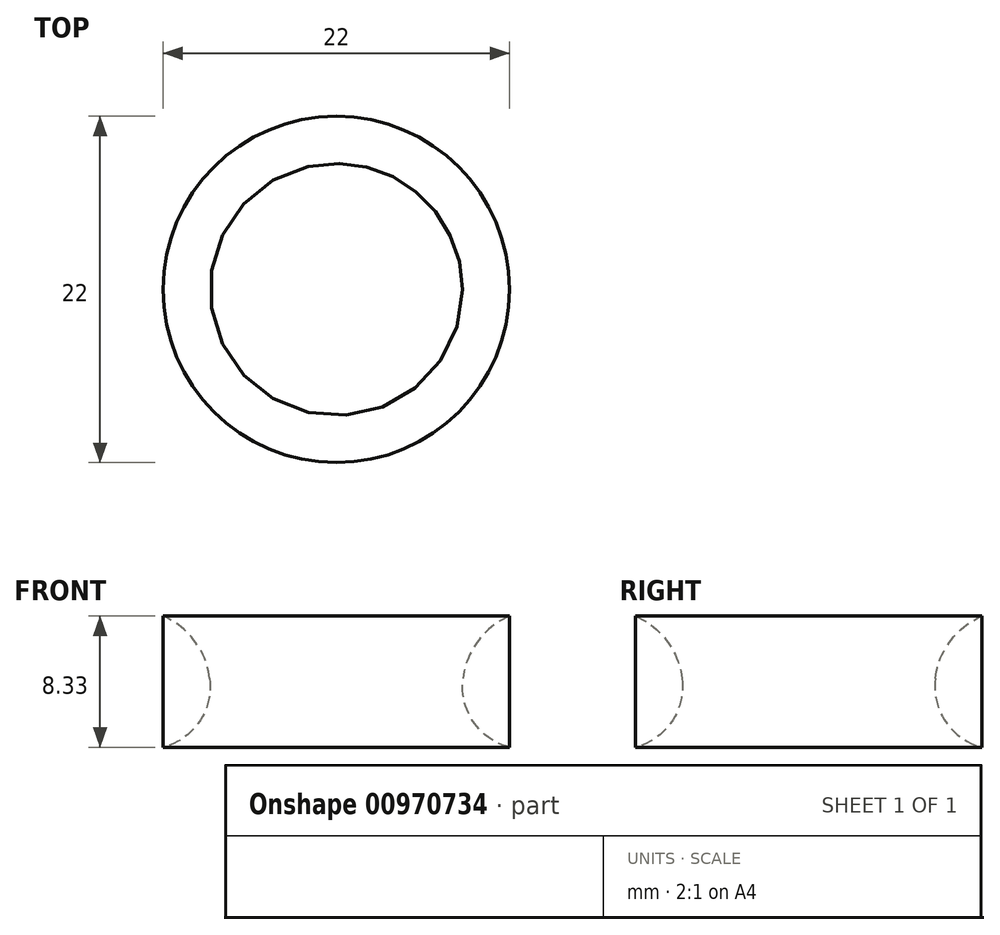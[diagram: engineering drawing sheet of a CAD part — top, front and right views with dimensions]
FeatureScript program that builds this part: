
annotation { "Feature Type Name" : "Feature", "Feature Type Description" : "" }
export const myFeature = defineFeature(function(context is Context, id is Id, definition is map)
    precondition{}
    {
        {
            var Q0;
            Q0=qCreatedBy(makeId("Top.planeOp"),FACE);
            var sketch = newSketch(context, id + "F0", { "sketchPlane" : qUnion([Q0])});
            skCircle(sketch, "E0", {"center": v(0, 0) * mm, "radius": 11 * mm});
            skCircle(sketch, "E1", {"center": v(0, 0) * mm, "radius": 8 * mm});
            skSolve(sketch);
        }
        {
            var Q0;
            Q0=makeQuery(id+"F0.imprint","IMPRINT",FACE,{"disambiguationData":[TD([[makeQuery(id+"F0.imprint","IMPRINT",EDGE,{"derivedFrom":sQuery(id+"F0.wireOp",EDGE,"E0")}),1.0]])]});
            extrude(context, id + "F1", {"entities" : qUnion([Q0]), "depth" : 8.33 * mm, "offsetDistance" : 25 * mm});
        }
        {
            var Q0;
            Q0=makeQuery(id+"F1.opExtrude","CAP_FACE",FACE,{"disambiguationData":[OSD([sQuery(id+"F0.wireOp",EDGE,"E0")])],"isStart":false});
            var sketch = newSketch(context, id + "F2", { "sketchPlane" : qUnion([Q0])});
            skCircle(sketch, "E2", {"center": v(0, 0) * mm, "radius": 11.53 * mm});
            skSolve(sketch);
        }
        {
            var Q0;
            Q0=makeQuery(id+"F2.imprint","IMPRINT",FACE,{"disambiguationData":[TD([[makeQuery(id+"F2.imprint","IMPRINT",EDGE,{"derivedFrom":sQuery(id+"F2.wireOp",EDGE,"E2")}),1.0]])]});
            extrude(context, id + "F3", {"entities" : qUnion([Q0]), "operationType" : NewBodyOperationType.REMOVE, "oppositeDirection" : true, "depth" : 25 * mm, "offsetDistance" : 25 * mm});
        }
        {
            var Q0;
            Q0=makeQuery(id+"F1.opExtrude","CAP_EDGE",EDGE,{"disambiguationData":[OSD([sQuery(id+"F0.wireOp",EDGE,"E1")])],"isStart":false});
            fillet(context, id + "F4", {"entities" : qUnion([Q0]), "radius" : 5 * mm, "tangentPropagation" : true, "allowEdgeOverflow" : false});
        }
        {
            var Q0;
            Q0=makeQuery(id+"F1.opExtrude","CAP_EDGE",EDGE,{"disambiguationData":[OSD([sQuery(id+"F0.wireOp",EDGE,"E1")])],"isStart":true});
            fillet(context, id + "F5", {"entities" : qUnion([Q0]), "radius" : 4 * mm, "tangentPropagation" : true, "allowEdgeOverflow" : false});
        }
    });
